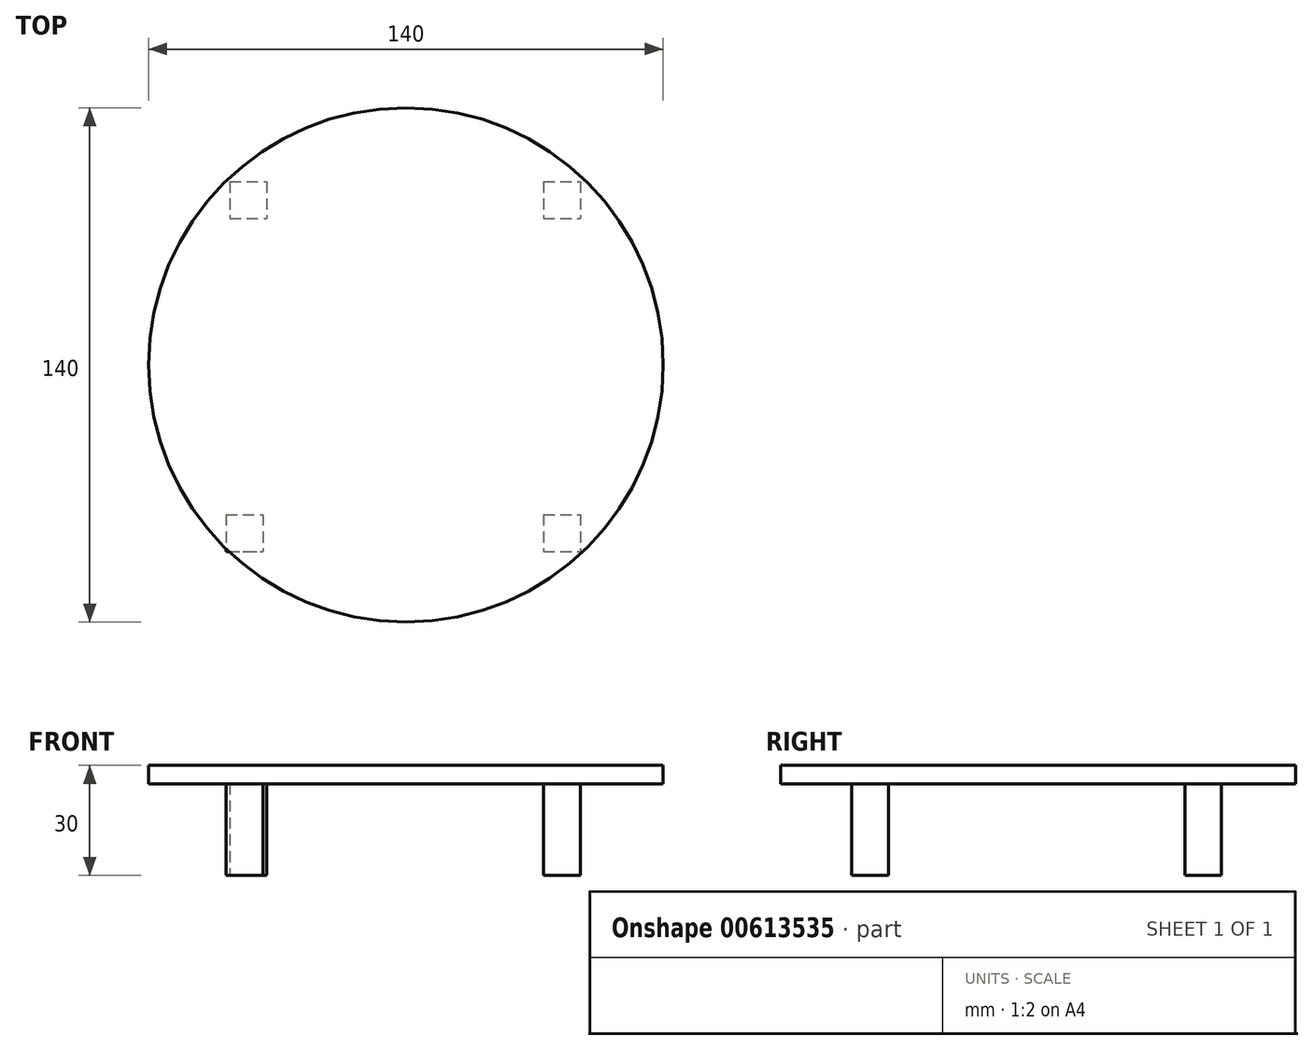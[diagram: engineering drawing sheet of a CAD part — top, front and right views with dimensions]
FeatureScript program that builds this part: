
annotation { "Feature Type Name" : "Feature", "Feature Type Description" : "" }
export const myFeature = defineFeature(function(context is Context, id is Id, definition is map)
    precondition{}
    {
        {
            var Q0;
            Q0=qCreatedBy(makeId("Top.planeOp"),FACE);
            var sketch = newSketch(context, id + "F0", { "sketchPlane" : qUnion([Q0])});
            skLineSegment(sketch, "E0.bottom", {"start": v(-47.9, 49.9) * mm, "end": v(-37.9, 49.9) * mm});
            skLineSegment(sketch, "E0.top", {"start": v(-47.9, 39.9) * mm, "end": v(-37.9, 39.9) * mm});
            skLineSegment(sketch, "E0.left", {"start": v(-47.9, 49.9) * mm, "end": v(-47.9, 39.9) * mm});
            skLineSegment(sketch, "E0.right", {"start": v(-37.9, 49.9) * mm, "end": v(-37.9, 39.9) * mm});
            skLineSegment(sketch, "E1.bottom", {"start": v(37.44, 49.9) * mm, "end": v(47.44, 49.9) * mm});
            skLineSegment(sketch, "E1.top", {"start": v(37.44, 39.9) * mm, "end": v(47.44, 39.9) * mm});
            skLineSegment(sketch, "E1.left", {"start": v(37.44, 49.9) * mm, "end": v(37.44, 39.9) * mm});
            skLineSegment(sketch, "E1.right", {"start": v(47.44, 49.9) * mm, "end": v(47.44, 39.9) * mm});
            skLineSegment(sketch, "E2.bottom", {"start": v(37.44, -40.76) * mm, "end": v(47.44, -40.76) * mm});
            skLineSegment(sketch, "E2.top", {"start": v(37.44, -50.76) * mm, "end": v(47.44, -50.76) * mm});
            skLineSegment(sketch, "E2.left", {"start": v(37.44, -40.76) * mm, "end": v(37.44, -50.76) * mm});
            skLineSegment(sketch, "E2.right", {"start": v(47.44, -40.76) * mm, "end": v(47.44, -50.76) * mm});
            skLineSegment(sketch, "E3.bottom", {"start": v(-48.9, -40.76) * mm, "end": v(-38.9, -40.76) * mm});
            skLineSegment(sketch, "E3.top", {"start": v(-48.9, -50.76) * mm, "end": v(-38.9, -50.76) * mm});
            skLineSegment(sketch, "E3.left", {"start": v(-48.9, -40.76) * mm, "end": v(-48.9, -50.76) * mm});
            skLineSegment(sketch, "E3.right", {"start": v(-38.9, -40.76) * mm, "end": v(-38.9, -50.76) * mm});
            skSolve(sketch);
        }
        {
            var Q0;
            Q0 = qSketchRegion(id + "F0", true);
            extrude(context, id + "F1", {"entities" : qUnion([Q0]), "depth" : 25 * mm, "offsetDistance" : 25 * mm});
        }
        {
            var Q0;
            Q0=makeQuery(id+"F1.opExtrude","CAP_FACE",FACE,{"disambiguationData":[OSD([sQuery(id+"F0.wireOp",EDGE,"E1.bottom"),sQuery(id+"F0.wireOp",EDGE,"E1.top"),sQuery(id+"F0.wireOp",EDGE,"E1.left"),sQuery(id+"F0.wireOp",EDGE,"E1.right")])],"isStart":false});
            var sketch = newSketch(context, id + "F2", { "sketchPlane" : qUnion([Q0])});
            skCircle(sketch, "E4", {"center": v(0, 0) * mm, "radius": 70 * mm});
            skSolve(sketch);
        }
        {
            var Q0;
            Q0 = qSketchRegion(id + "F2", true);
            extrude(context, id + "F3", {"entities" : qUnion([Q0]), "depth" : 5 * mm, "offsetDistance" : 25 * mm});
        }
    });
